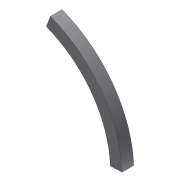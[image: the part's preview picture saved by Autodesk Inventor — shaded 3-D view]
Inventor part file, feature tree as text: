
AUTODESK INVENTOR PART (.ipt)
format: ipt  version: 2012 (Build 160160000, 160)  size: 93,184 bytes
history: native  units: in
note: dims shown in document units (in); Inventor stores cm internally (conversion verified against a paired STEP export)
features: extrude x2, sketch x2, shell x1
ambient origin geometry x8: Origin, YZ Plane, XZ Plane, XY Plane, X Axis, Y Axis, Z Axis, Center Point
bodies: Solid1 (feature_tree)
feature tree (5):
  extrude  "Extrusion1"  Depth=1.0in
  shell  "Shell1"  Thickness=8.5in
  extrude  "Extrusion2"  Depth=0.0625in
  sketch  "Sketch1"  dims[d0=0.5085in d1=1.0in d2=8.5in]
  sketch  "Sketch2"  dims[d3=1.0in d4=0.0in d5=0.0625in d6=1.0in d7=1.0in d8=0.0in]
